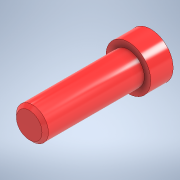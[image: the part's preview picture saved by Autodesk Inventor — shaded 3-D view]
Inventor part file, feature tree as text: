
AUTODESK INVENTOR PART (.ipt)
format: ipt  version: 2022 (Build 260153000, 153)  size: 112,128 bytes
history: native  units: in
note: dims shown in document units (in); Inventor stores cm internally (conversion verified against a paired STEP export)
features: extrude x2, sketch x2, chamfer x1
ambient origin geometry x8: Origin, YZ Plane, XZ Plane, XY Plane, X Axis, Y Axis, Z Axis, Center Point
bodies: Solid1 (feature_tree)
feature tree (5):
  extrude  "Extrusion1"  Depth=0.2756in TaperAngle=0.0deg
  extrude  "Extrusion2"  Depth=1.2205in TaperAngle=0.0deg
  chamfer  "Chamfer1"  Distance=0.0394in Angle=45.0deg
  sketch  "Sketch1"  dims[d0=0.5512in d1=0.2756in d2=0.0in]
  sketch  "Sketch2"  dims[d3=0.3937in d4=1.2205in d5=0.0in d6=0.0394in d7=0.0787in d8=45.0deg]
